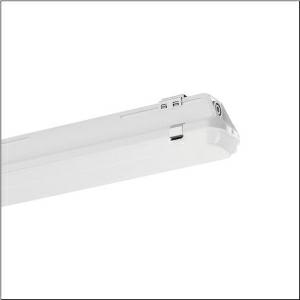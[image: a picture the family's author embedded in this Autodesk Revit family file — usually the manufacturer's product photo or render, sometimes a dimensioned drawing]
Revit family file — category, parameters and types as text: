
# Revit family: monsun_r__21_51fb10mp480c_93ab
name_source: partatom
category: Lighting Fixtures
units: mm (PartAtom-declared; Revit-internal decimal feet)

## family parameters
Cut with Voids When Loaded = No
Host = Face
Light Source = No
Part Type = Normal
Room Calculation Point = No
Round Connector Dimension = Use Diameter
Shared = No

## types (1)
- --- (1 x LED, 8550 lm, 45.6 W, 4000K)
    Apparent Load = 46 VA
    CIE Flux Codes = 47 77 93 94 100
    Color Rendering = 80
    Color Temperature = 4000K
    Default Elevation = 1800 mm
    Description = Monsun® 21, damp-proof luminaire, chain hanger, primary optical cover: enclosure, of PMMA, light emission: direct distribution, primary light characteristic: symmetric, installation type: suspended mounting, surface-mounted, horizontal mounting, vertical mounting, LED, rated luminous flux: 8.550lm, luminous efficacy: 188lm/W, light colour: 840, colour temperature: 4000K, control gear: ON/OFF Multilumen, with terminal, 3-pole, max. 2.5mm², mains connection: 220..240V, AC, 50/60Hz, rated input power: 46W, housing, of glass-fibre reinforced polyester, uncoated, bright grey, incl. chain hanger, length: 1.590mm, width: 90mm, height: 88mm, clip for enclosure, of stainless steel (V2A), ceiling mounting element, of stainless steel (V2A), chain hanger, of stainless steel (V2A), protection rating (complete): IP66, insulation class (complete): insulation class I (protective earthing), certification: CE, ENEC, VDE, UKCA, protection symbol: D, impact resistance: IK04, permissible operating ambient temperature: -25..+35°C, standard: EN 50419, EN 60598-2-1, corresponds to IFS (International Featured Standards) requirements for safety and quality in the food industry, for indoor or canopied outdoor use, no direct snow, no direct sun, no direct rain, LABS conformity tested according to VDMA 24364:2018-05, contact your sales advisor before using the luminaires in applications with unclear chemical exposure, large temperature fluctuations or condensation-forming humidity, packaging unit: 1 piece
    Height = 89 mm
    Lamp = 1 x LED
    Lamp Light Flux = 8550 lm
    Lamp Power = 45.6 W
    Lamp count = 1
    Length = 1590 mm
    Luminous efficacy = 188 lm/W
    Manufacturer = Siteco
    ModVariant = No
    Model = 51FB10MP480C
    Mounting Place = Ceiling
    Mounting Type = Surface mounted
    Number of Poles = 1
    OnlyDefault = Yes
    Power Factor = 1
    Product Name = Monsun® 21
    Product group = damp-proof luminaire
    ProductGroupID = 300
    Protection Class = Protection class I
    Protection Degree = IP 66
    RLX_Detail_Level = 1
    RLX_Emergency_Light_Flux = 0 lm
    RLX_Emergency_Type = 0
    RLX_Emergency_Type_DB = No
    RlxData = <blob elided: 89789 chars, md5=bce4cc24>
    Socket = socket
    Standby Power = 0 W
    System Light Flux = 8550 lm
    System Power = 46 W
    Type Comments = factory setting: luminous flux: 100 % | (A | C | E) | 106 mA
    Type Image = l_1319656.jpg
    URL = http://relux.com
    VarID = @adj_031794
    Voltage = 0 V
    Weight = 0.00 kg
    Width = 90 mm

## geometry (parser evidence)
native form markers: Blend x4, Sweep x12
no freeform markers — native parametric forms only
